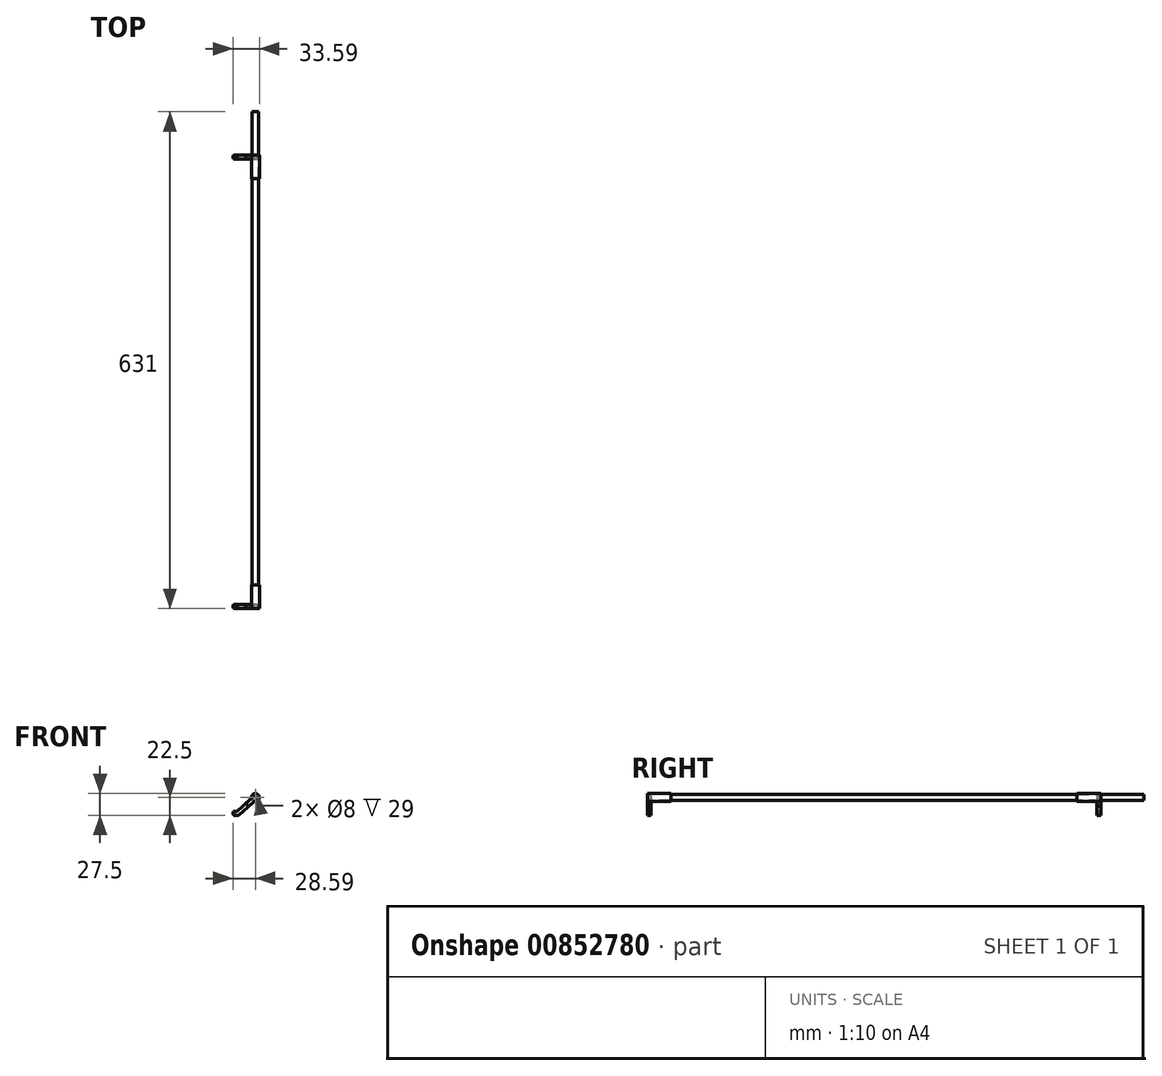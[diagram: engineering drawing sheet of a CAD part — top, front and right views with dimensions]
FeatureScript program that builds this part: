
annotation { "Feature Type Name" : "Feature", "Feature Type Description" : "" }
export const myFeature = defineFeature(function(context is Context, id is Id, definition is map)
    precondition{}
    {
        {
            var Q0;
            Q0=qCreatedBy(makeId("Front.planeOp"),FACE);
            cPlane(context, id + "F0", {"entities" : qUnion([Q0]), "cplaneType" : CPlaneType.OFFSET, "offset" : 576 * mm, "width" : 150 * mm, "height" : 150 * mm});
        }
        {
            var Q0;
            Q0=qCreatedBy(makeId("Front.planeOp"),FACE);
            var sketch = newSketch(context, id + "F1", { "sketchPlane" : qUnion([Q0])});
            skCircle(sketch, "E0", {"center": v(0, 0) * mm, "radius": 5 * mm});
            skLineSegment(sketch, "E1", {"start": v(-4.86, -1.2) * mm, "end": v(-12.37, -7.8) * mm});
            skLineSegment(sketch, "E2", {"start": v(-1.4, -4.8) * mm, "end": v(-8.9, -11.4) * mm});
            skLineSegment(sketch, "E3", {"start": v(-12.37, -7.8) * mm, "end": v(-8.9, -11.4) * mm});
            skSolve(sketch);
        }
        {
            var Q0;
            {var subQ0=sQuery(id+"F1.wireOp",EDGE,"E0");var subQ1=makeQuery(id+"F1.imprint","INTERSECT",VERTEX,{"derivedFrom":[subQ0,sQuery(id+"F1.wireOp",EDGE,"E1")]});Q0=makeQuery(id+"F1.imprint","IMPRINT",FACE,{"disambiguationData":[TD([[makeQuery(id+"F1.imprint","IMPRINT",EDGE,{"disambiguationData":[TD([[subQ1,-1.0]])],"derivedFrom":subQ0}),1.0]])]});}
            extrude(context, id + "F2", {"entities" : qUnion([Q0]), "depth" : 30 * mm, "offsetDistance" : 25 * mm});
        }
        {
            var Q0;
            {var subQ0=sQuery(id+"F1.wireOp",EDGE,"E1");Q0=makeQuery(id+"F1.imprint","IMPRINT",FACE,{"disambiguationData":[TD([[makeQuery(id+"F1.imprint","IMPRINT",EDGE,{"derivedFrom":subQ0}),1.0]])]});}
            extrude(context, id + "F3", {"entities" : qUnion([Q0]), "operationType" : NewBodyOperationType.ADD, "depth" : 5 * mm, "offsetDistance" : 25 * mm});
        }
        {
            var Q0;
            Q0=qCreatedBy(id+"F0.planeOp",FACE);
            var sketch = newSketch(context, id + "F4", { "sketchPlane" : qUnion([Q0])});
            skCircle(sketch, "E4", {"center": v(0, 0) * mm, "radius": 5 * mm});
            skLineSegment(sketch, "E5", {"start": v(-4.86, -1.2) * mm, "end": v(-12.37, -7.8) * mm});
            skLineSegment(sketch, "E6", {"start": v(-1.4, -4.8) * mm, "end": v(-8.9, -11.4) * mm});
            skLineSegment(sketch, "E7", {"start": v(-12.37, -7.8) * mm, "end": v(-8.9, -11.4) * mm});
            skSolve(sketch);
        }
        {
            var Q0;
            {var subQ0=sQuery(id+"F4.wireOp",EDGE,"E4");var subQ1=makeQuery(id+"F4.imprint","INTERSECT",VERTEX,{"derivedFrom":[subQ0,sQuery(id+"F4.wireOp",EDGE,"E5")]});Q0=makeQuery(id+"F4.imprint","IMPRINT",FACE,{"disambiguationData":[TD([[makeQuery(id+"F4.imprint","IMPRINT",EDGE,{"disambiguationData":[TD([[subQ1,-1.0]])],"derivedFrom":subQ0}),1.0]])]});}
            extrude(context, id + "F5", {"entities" : qUnion([Q0]), "oppositeDirection" : true, "depth" : 30 * mm, "offsetDistance" : 25 * mm});
        }
        {
            var Q0;
            {var subQ0=sQuery(id+"F4.wireOp",EDGE,"E5");Q0=makeQuery(id+"F4.imprint","IMPRINT",FACE,{"disambiguationData":[TD([[makeQuery(id+"F4.imprint","IMPRINT",EDGE,{"derivedFrom":subQ0}),1.0]])]});}
            extrude(context, id + "F6", {"entities" : qUnion([Q0]), "operationType" : NewBodyOperationType.ADD, "oppositeDirection" : true, "depth" : 5 * mm, "offsetDistance" : 25 * mm});
        }
        {
            var Q0;
            Q0=makeQuery(id+"F5.opExtrude","CAP_FACE",FACE,{"disambiguationData":[OSD([sQuery(id+"F4.wireOp",EDGE,"E4")])],"isStart":false});
            shell(context, id + "F7", {"entities" : qUnion([Q0]), "thickness" : 1 * mm});
        }
        {
            var Q0;
            Q0=makeQuery(id+"F2.opExtrude","CAP_FACE",FACE,{"disambiguationData":[OSD([sQuery(id+"F1.wireOp",EDGE,"E0")])],"isStart":false});
            shell(context, id + "F8", {"entities" : qUnion([Q0]), "thickness" : 1 * mm});
        }
        {
            var Q0;
            {var subQ0=sQuery(id+"F4.wireOp",EDGE,"E7");var subQ1=sQuery(id+"F4.wireOp",EDGE,"E6");var subQ2=sQuery(id+"F4.wireOp",EDGE,"E5");var subQ3=sQuery(id+"F4.wireOp",EDGE,"E4");Q0=makeQuery(id+"F7.opShell","OFFSET_FACE",FACE,{"disambiguationData":[OSD([subQ3,subQ2,subQ1,subQ0]),TDD([makeQuery(id+"F6.boolean.opBoolean","MERGE",FACE,{"derivedFrom":[makeQuery(id+"F5.opExtrude","CAP_FACE",FACE,{"disambiguationData":[OSD([subQ3])],"isStart":true}),makeQuery(id+"F6.opExtrude","CAP_FACE",FACE,{"disambiguationData":[OSD([subQ3,subQ2,subQ1,subQ0])],"isStart":true})]})])]});}
            var sketch = newSketch(context, id + "F9", { "sketchPlane" : qUnion([Q0])});
            skCircle(sketch, "E8", {"center": v(0, 0) * mm, "radius": 4 * mm});
            skSolve(sketch);
        }
        {
            var Q0;
            Q0 = qSketchRegion(id + "F9", true);
            extrude(context, id + "F10", {"entities" : qUnion([Q0]), "depth" : 630 * mm, "offsetDistance" : 25 * mm});
        }
        {
            var Q0;
            Q0=qCreatedBy(id+"F0.planeOp",FACE);
            var sketch = newSketch(context, id + "F11", { "sketchPlane" : qUnion([Q0])});
            skLineSegment(sketch, "E9", {"start": v(0, 0) * mm, "end": v(-22.53, -19.8) * mm});
            skLineSegment(sketch, "E10", {"start": v(-22.53, -19.8) * mm, "end": v(-27.53, -19.8) * mm});
            skSolve(sketch);
        }
        {
            var Q0;
            Q0=makeQuery(id+"F6.opExtrude","SWEPT_FACE",FACE,{"disambiguationData":[OSD([sQuery(id+"F4.wireOp",EDGE,"E7")])]});
            var Q1;
            Q1=sQuery(id+"F11.wireOp",EDGE,"E9");
            var Q2;
            Q2=sQuery(id+"F11.wireOp",EDGE,"E10");
            sweep(context, id + "F12", {"profiles" : qUnion([Q0]), "path" : qUnion([Q1, Q2])});
        }
        {
            var Q0;
            Q0=makeQuery(id+"F3.opExtrude","SWEPT_FACE",FACE,{"disambiguationData":[OSD([sQuery(id+"F1.wireOp",EDGE,"E3")])]});
            var Q1;
            Q1=sQuery(id+"F11.wireOp",EDGE,"E9");
            var Q2;
            Q2=sQuery(id+"F11.wireOp",EDGE,"E10");
            sweep(context, id + "F13", {"profiles" : qUnion([Q0]), "path" : qUnion([Q1, Q2])});
        }
        {
            var Q0;
            Q0=makeQuery(id+"F12.opSweep","CAP_FACE",FACE,{"disambiguationData":[OSD([sQuery(id+"F4.wireOp",EDGE,"E7"),sQuery(id+"F11.wireOp",VERTEX,"E10.end")])],"isStart":false});
            var sketch = newSketch(context, id + "F14", { "sketchPlane" : qUnion([Q0])});
            skCircle(sketch, "E11", {"center": v(573.5, -18.78) * mm, "radius": 1.5 * mm});
            skSolve(sketch);
        }
        {
            var Q0;
            Q0=makeQuery(id+"F14.imprint","IMPRINT",FACE,{"disambiguationData":[TD([[makeQuery(id+"F14.imprint","IMPRINT",EDGE,{"derivedFrom":sQuery(id+"F14.wireOp",EDGE,"E11")}),1.0]])]});
            extrude(context, id + "F15", {"entities" : qUnion([Q0]), "operationType" : NewBodyOperationType.REMOVE, "oppositeDirection" : true, "depth" : 3 * mm, "offsetDistance" : 25 * mm});
        }
        {
            var Q0;
            Q0=makeQuery(id+"F13.opSweep","CAP_FACE",FACE,{"disambiguationData":[OSD([sQuery(id+"F1.wireOp",EDGE,"E3"),sQuery(id+"F11.wireOp",VERTEX,"E10.end")])],"isStart":false});
            var sketch = newSketch(context, id + "F16", { "sketchPlane" : qUnion([Q0])});
            skCircle(sketch, "E12", {"center": v(2.5, -18.78) * mm, "radius": 1.5 * mm});
            skSolve(sketch);
        }
        {
            var Q0;
            Q0=makeQuery(id+"F16.imprint","IMPRINT",FACE,{"disambiguationData":[TD([[makeQuery(id+"F16.imprint","IMPRINT",EDGE,{"derivedFrom":sQuery(id+"F16.wireOp",EDGE,"E12")}),1.0]])]});
            extrude(context, id + "F17", {"entities" : qUnion([Q0]), "operationType" : NewBodyOperationType.REMOVE, "oppositeDirection" : true, "depth" : 3 * mm, "offsetDistance" : 25 * mm});
        }
        {
            var Q0;
            Q0=makeQuery(id+"F17.boolean.opBoolean","COPY",FACE,{"derivedFrom":makeQuery(id+"F17.opExtrude","CAP_FACE",FACE,{"disambiguationData":[OSD([sQuery(id+"F16.wireOp",EDGE,"E12")])],"isStart":false})});
            extrude(context, id + "F18", {"entities" : qUnion([Q0]), "operationType" : NewBodyOperationType.ADD, "depth" : 4 * mm, "offsetDistance" : 25 * mm});
        }
        {
            var Q0;
            Q0=makeQuery(id+"F15.boolean.opBoolean","COPY",FACE,{"derivedFrom":makeQuery(id+"F15.opExtrude","CAP_FACE",FACE,{"disambiguationData":[OSD([sQuery(id+"F14.wireOp",EDGE,"E11")])],"isStart":false})});
            extrude(context, id + "F19", {"entities" : qUnion([Q0]), "operationType" : NewBodyOperationType.ADD, "depth" : 4 * mm, "offsetDistance" : 25 * mm});
        }
    });
